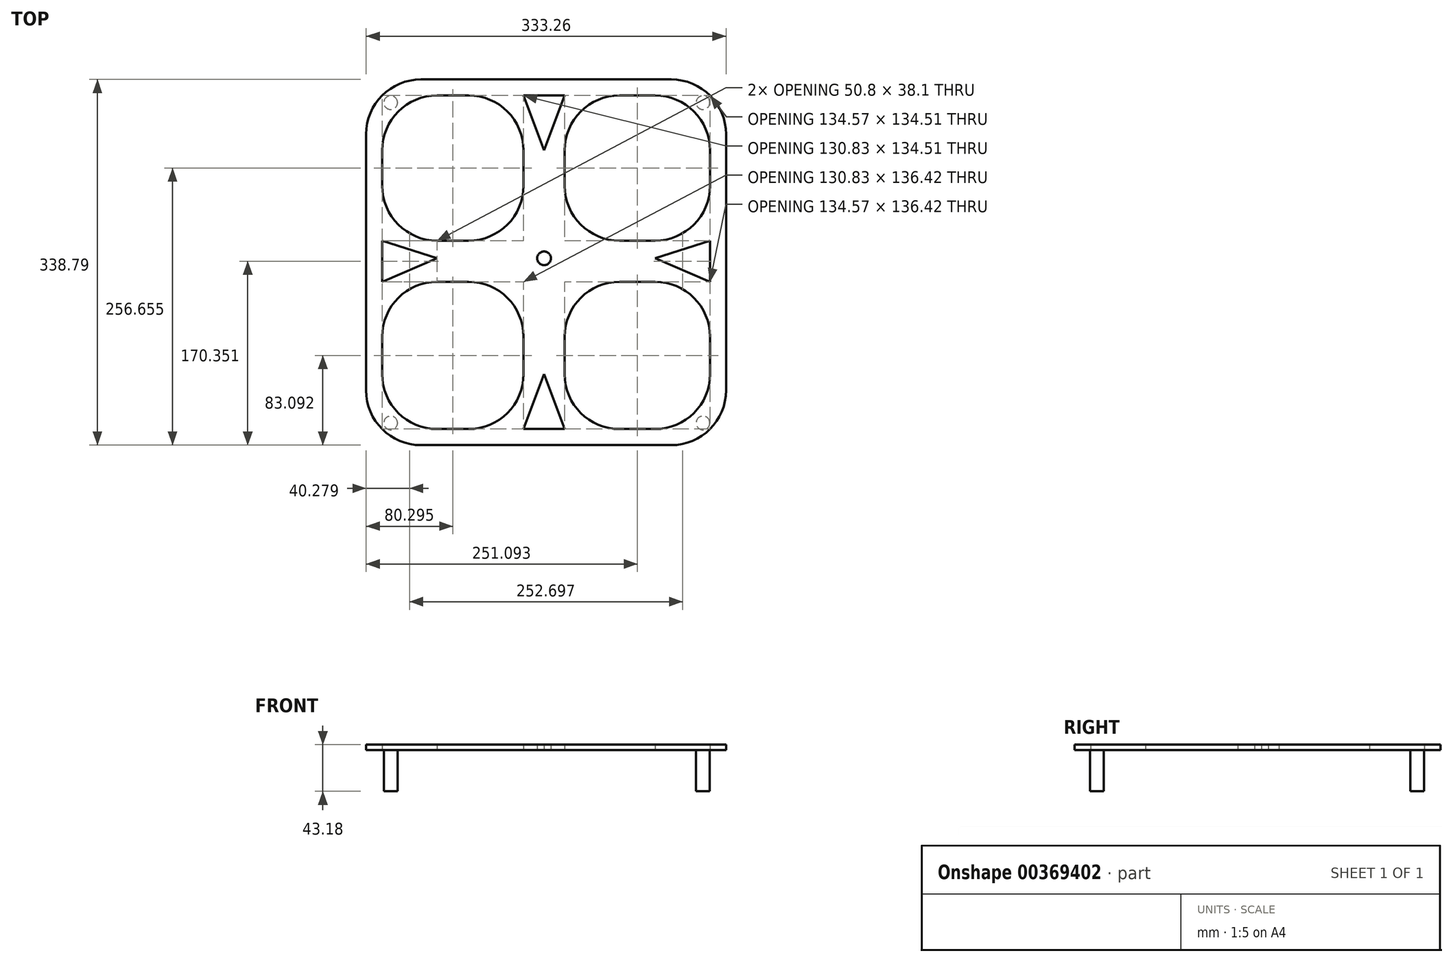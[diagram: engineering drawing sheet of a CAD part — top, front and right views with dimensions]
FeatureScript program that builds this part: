
annotation { "Feature Type Name" : "Feature", "Feature Type Description" : "" }
export const myFeature = defineFeature(function(context is Context, id is Id, definition is map)
    precondition{}
    {
        {
            var Q0;
            Q0=qCreatedBy(makeId("Top.planeOp"),FACE);
            var sketch = newSketch(context, id + "F0", { "sketchPlane" : qUnion([Q0])});
            skLineSegment(sketch, "E0.bottom", {"start": v(102.82, 16.36) * mm, "end": v(69.85, 16.36) * mm});
            skLineSegment(sketch, "E0.top", {"start": v(102.82, -21.74) * mm, "end": v(69.85, -21.74) * mm});
            skPoint(sketch, "E0.middle", {"position": v(0, 0) * mm});
            skLineSegment(sketch, "E1.left", {"start": v(19.05, 100.07) * mm, "end": v(19.05, 67.16) * mm});
            skLineSegment(sketch, "E1.right", {"start": v(-19.05, 100.07) * mm, "end": v(-19.05, 67.16) * mm});
            skPoint(sketch, "E2", {"position": v(-19.05, 16.36) * mm});
            skPoint(sketch, "E3", {"position": v(19.05, 16.36) * mm});
            skPoint(sketch, "E4", {"position": v(19.05, -21.74) * mm});
            skPoint(sketch, "E5", {"position": v(-19.05, -21.74) * mm});
            skLineSegment(sketch, "E6.trimOffspring", {"start": v(-19.05, -72.54) * mm, "end": v(-19.05, -107.36) * mm});
            skLineSegment(sketch, "E7.trimOffspring", {"start": v(-69.85, 16.36) * mm, "end": v(-99.08, 16.36) * mm});
            skLineSegment(sketch, "E8.trimOffspring", {"start": v(19.05, -72.54) * mm, "end": v(19.05, -107.36) * mm});
            skLineSegment(sketch, "E9.trimOffspring", {"start": v(-69.85, -21.74) * mm, "end": v(-99.08, -21.74) * mm});
            skCircle(sketch, "E10", {"center": v(0, 0) * mm, "radius": 6.35 * mm});
            skArc(sketch, "E11.filletArc", {"start": v(-25.4, 16.36) * mm, "mid": v(-20.1, 19.2) * mm, "end": v(-19.55, 25.19) * mm});
            skArc(sketch, "E12.filletArc", {"start": v(-69.85, 16.36) * mm, "mid": v(-33.93, 31.24) * mm, "end": v(-19.05, 67.16) * mm});
            skArc(sketch, "E13.filletArc", {"start": v(19.05, 67.16) * mm, "mid": v(33.93, 31.24) * mm, "end": v(69.85, 16.36) * mm});
            skArc(sketch, "E14.filletArc", {"start": v(69.85, -21.74) * mm, "mid": v(33.93, -36.62) * mm, "end": v(19.05, -72.54) * mm});
            skArc(sketch, "E15.filletArc", {"start": v(-19.05, -72.54) * mm, "mid": v(-33.93, -36.62) * mm, "end": v(-69.85, -21.74) * mm});
            skLineSegment(sketch, "E16", {"start": v(69.85, 150.87) * mm, "end": v(102.82, 150.87) * mm});
            skLineSegment(sketch, "E17", {"start": v(153.62, 100.07) * mm, "end": v(153.62, 67.16) * mm});
            skPoint(sketch, "E18.visualSharp", {"position": v(153.62, 16.36) * mm});
            skArc(sketch, "E18.filletArc", {"start": v(102.82, 16.36) * mm, "mid": v(138.74, 31.24) * mm, "end": v(153.62, 67.16) * mm});
            skPoint(sketch, "E19.visualSharp", {"position": v(19.05, 150.87) * mm});
            skArc(sketch, "E19.filletArc", {"start": v(69.85, 150.87) * mm, "mid": v(33.93, 136) * mm, "end": v(19.05, 100.07) * mm});
            skPoint(sketch, "E20.visualSharp", {"position": v(153.62, 150.87) * mm});
            skArc(sketch, "E20.filletArc", {"start": v(153.62, 100.07) * mm, "mid": v(138.74, 136) * mm, "end": v(102.82, 150.87) * mm});
            skLineSegment(sketch, "E21", {"start": v(-149.88, 67.16) * mm, "end": v(-149.88, 100.07) * mm});
            skLineSegment(sketch, "E22", {"start": v(-99.08, 150.87) * mm, "end": v(-69.85, 150.87) * mm});
            skPoint(sketch, "E23.visualSharp", {"position": v(-149.88, 16.36) * mm});
            skArc(sketch, "E23.filletArc", {"start": v(-149.88, 67.16) * mm, "mid": v(-135, 31.24) * mm, "end": v(-99.08, 16.36) * mm});
            skPoint(sketch, "E24.visualSharp", {"position": v(-149.88, 150.87) * mm});
            skArc(sketch, "E24.filletArc", {"start": v(-99.08, 150.87) * mm, "mid": v(-135, 136) * mm, "end": v(-149.88, 100.07) * mm});
            skPoint(sketch, "E25.visualSharp", {"position": v(-19.05, 150.87) * mm});
            skArc(sketch, "E25.filletArc", {"start": v(-19.05, 100.07) * mm, "mid": v(-33.93, 136) * mm, "end": v(-69.85, 150.87) * mm});
            skLineSegment(sketch, "E26", {"start": v(-149.88, -72.54) * mm, "end": v(-149.88, -107.36) * mm});
            skLineSegment(sketch, "E27", {"start": v(-99.08, -158.16) * mm, "end": v(-69.85, -158.16) * mm});
            skPoint(sketch, "E28.visualSharp", {"position": v(-149.88, -158.16) * mm});
            skArc(sketch, "E28.filletArc", {"start": v(-149.88, -107.36) * mm, "mid": v(-135, -143.28) * mm, "end": v(-99.08, -158.16) * mm});
            skPoint(sketch, "E29.visualSharp", {"position": v(-19.05, -158.16) * mm});
            skPoint(sketch, "E30.visualSharp", {"position": v(-149.88, -21.74) * mm});
            skArc(sketch, "E30.filletArc", {"start": v(-99.08, -21.74) * mm, "mid": v(-135, -36.62) * mm, "end": v(-149.88, -72.54) * mm});
            skArc(sketch, "E31.filletArc", {"start": v(-69.85, -158.16) * mm, "mid": v(-33.93, -143.28) * mm, "end": v(-19.05, -107.36) * mm});
            skLineSegment(sketch, "E32", {"start": v(69.85, -158.16) * mm, "end": v(102.82, -158.16) * mm});
            skLineSegment(sketch, "E33", {"start": v(153.62, -107.36) * mm, "end": v(153.62, -72.54) * mm});
            skPoint(sketch, "E34.visualSharp", {"position": v(19.05, -158.16) * mm});
            skArc(sketch, "E34.filletArc", {"start": v(19.05, -107.36) * mm, "mid": v(33.93, -143.28) * mm, "end": v(69.85, -158.16) * mm});
            skPoint(sketch, "E35.visualSharp", {"position": v(153.62, -158.16) * mm});
            skArc(sketch, "E35.filletArc", {"start": v(102.82, -158.16) * mm, "mid": v(138.74, -143.28) * mm, "end": v(153.62, -107.36) * mm});
            skPoint(sketch, "E36.visualSharp", {"position": v(153.62, -21.74) * mm});
            skArc(sketch, "E36.filletArc", {"start": v(153.62, -72.54) * mm, "mid": v(138.74, -36.62) * mm, "end": v(102.82, -21.74) * mm});
            skLineSegment(sketch, "E37", {"start": v(-113.96, -173.04) * mm, "end": v(117.7, -173.04) * mm});
            skLineSegment(sketch, "E38", {"start": v(168.5, -122.24) * mm, "end": v(168.5, 114.95) * mm});
            skLineSegment(sketch, "E39", {"start": v(117.7, 165.75) * mm, "end": v(-113.96, 165.75) * mm});
            skLineSegment(sketch, "E40", {"start": v(-164.76, 165.75) * mm, "end": v(-164.76, 157.7) * mm});
            skLineSegment(sketch, "E41", {"start": v(-164.76, -122.24) * mm, "end": v(-164.76, 114.95) * mm});
            skPoint(sketch, "E42.visualSharp", {"position": v(-164.76, 165.75) * mm});
            skArc(sketch, "E42.filletArc", {"start": v(-113.96, 165.75) * mm, "mid": v(-149.88, 150.87) * mm, "end": v(-164.76, 114.95) * mm});
            skPoint(sketch, "E43.visualSharp", {"position": v(168.5, 165.75) * mm});
            skArc(sketch, "E43.filletArc", {"start": v(168.5, 114.95) * mm, "mid": v(153.62, 150.87) * mm, "end": v(117.7, 165.75) * mm});
            skPoint(sketch, "E44.visualSharp", {"position": v(168.5, -173.04) * mm});
            skArc(sketch, "E44.filletArc", {"start": v(117.7, -173.04) * mm, "mid": v(153.62, -158.16) * mm, "end": v(168.5, -122.24) * mm});
            skPoint(sketch, "E45.visualSharp", {"position": v(-164.76, -173.04) * mm});
            skArc(sketch, "E45.filletArc", {"start": v(-164.76, -122.24) * mm, "mid": v(-149.88, -158.16) * mm, "end": v(-113.96, -173.04) * mm});
            skLineSegment(sketch, "E46", {"start": v(0, -107.36) * mm, "end": v(-19.05, -158.16) * mm});
            skLineSegment(sketch, "E47", {"start": v(19.05, -158.16) * mm, "end": v(-19.05, -158.16) * mm});
            skLineSegment(sketch, "E48", {"start": v(19.05, -158.16) * mm, "end": v(0, -107.36) * mm});
            skLineSegment(sketch, "E49", {"start": v(0, 100.07) * mm, "end": v(-19.05, 150.87) * mm});
            skLineSegment(sketch, "E50", {"start": v(-19.05, 150.87) * mm, "end": v(19.05, 150.87) * mm});
            skLineSegment(sketch, "E51", {"start": v(19.05, 150.87) * mm, "end": v(0, 100.07) * mm});
            skLineSegment(sketch, "E52", {"start": v(-149.88, 16.36) * mm, "end": v(-149.88, -21.74) * mm});
            skLineSegment(sketch, "E53", {"start": v(102.82, 0) * mm, "end": v(153.62, 16.36) * mm});
            skLineSegment(sketch, "E54", {"start": v(153.62, -21.74) * mm, "end": v(153.62, 16.36) * mm});
            skLineSegment(sketch, "E55", {"start": v(153.62, -21.74) * mm, "end": v(102.82, 0) * mm});
            skLineSegment(sketch, "E56", {"start": v(-99.08, 0) * mm, "end": v(-149.88, -21.74) * mm});
            skLineSegment(sketch, "E57", {"start": v(-149.88, 16.36) * mm, "end": v(-99.08, 0) * mm});
            skSolve(sketch);
        }
        {
            var Q0;
            Q0=makeQuery(id+"F0.imprint","IMPRINT",FACE,{"disambiguationData":[TD([[makeQuery(id+"F0.imprint","IMPRINT",EDGE,{"derivedFrom":sQuery(id+"F0.wireOp",EDGE,"E0.bottom")}),1.0]])]});
            var Q1;
            Q1=makeQuery(id+"F0.imprint","IMPRINT",FACE,{"disambiguationData":[TD([[makeQuery(id+"F0.imprint","IMPRINT",EDGE,{"derivedFrom":sQuery(id+"F0.wireOp",EDGE,"HhHGXukK-88LZ-Qlhe-yOUI-ivqigiWirlnT")}),-1.0]])]});
            var Q2;
            Q2=makeQuery(id+"F0.imprint","IMPRINT",FACE,{"disambiguationData":[TD([[makeQuery(id+"F0.imprint","IMPRINT",EDGE,{"derivedFrom":sQuery(id+"F0.wireOp",EDGE,"GWZDvsel-j2r0-KArF-ZehE-5JIaTQembRwq")}),-1.0]])]});
            var Q3;
            Q3=makeQuery(id+"F0.imprint","IMPRINT",FACE,{"disambiguationData":[TD([[makeQuery(id+"F0.imprint","IMPRINT",EDGE,{"derivedFrom":sQuery(id+"F0.wireOp",EDGE,"nUYmWv30-9dqW-i0KR-sggg-cQleaPBZfBGV")}),-1.0]])]});
            var Q4;
            Q4=makeQuery(id+"F0.imprint","IMPRINT",FACE,{"disambiguationData":[TD([[makeQuery(id+"F0.imprint","IMPRINT",EDGE,{"derivedFrom":sQuery(id+"F0.wireOp",EDGE,"eROQzvXG-G305-7KOf-UkAC-neXF0GO081Xd")}),-1.0]])]});
            extrude(context, id + "F1", {"entities" : qUnion([Q0, Q1, Q2, Q3, Q4]), "depth" : 5.08 * mm});
        }
        {
            var Q0;
            Q0=qCreatedBy(makeId("Top.planeOp"),FACE);
            var sketch = newSketch(context, id + "F2", { "sketchPlane" : qUnion([Q0])});
            skCircle(sketch, "E58", {"center": v(-142.03, -152.5) * mm, "radius": 6.35 * mm});
            skCircle(sketch, "E59", {"center": v(-142.03, 144.24) * mm, "radius": 6.35 * mm});
            skCircle(sketch, "E60", {"center": v(147.1, 144.24) * mm, "radius": 6.35 * mm});
            skCircle(sketch, "E61", {"center": v(147.1, -152.5) * mm, "radius": 6.35 * mm});
            skSolve(sketch);
        }
        {
            var Q0;
            Q0=qSketchRegion(id+"F2",true);
            extrude(context, id + "F3", {"entities" : qUnion([Q0]), "operationType" : NewBodyOperationType.ADD, "oppositeDirection" : true, "depth" : 38.1 * mm});
        }
    });
